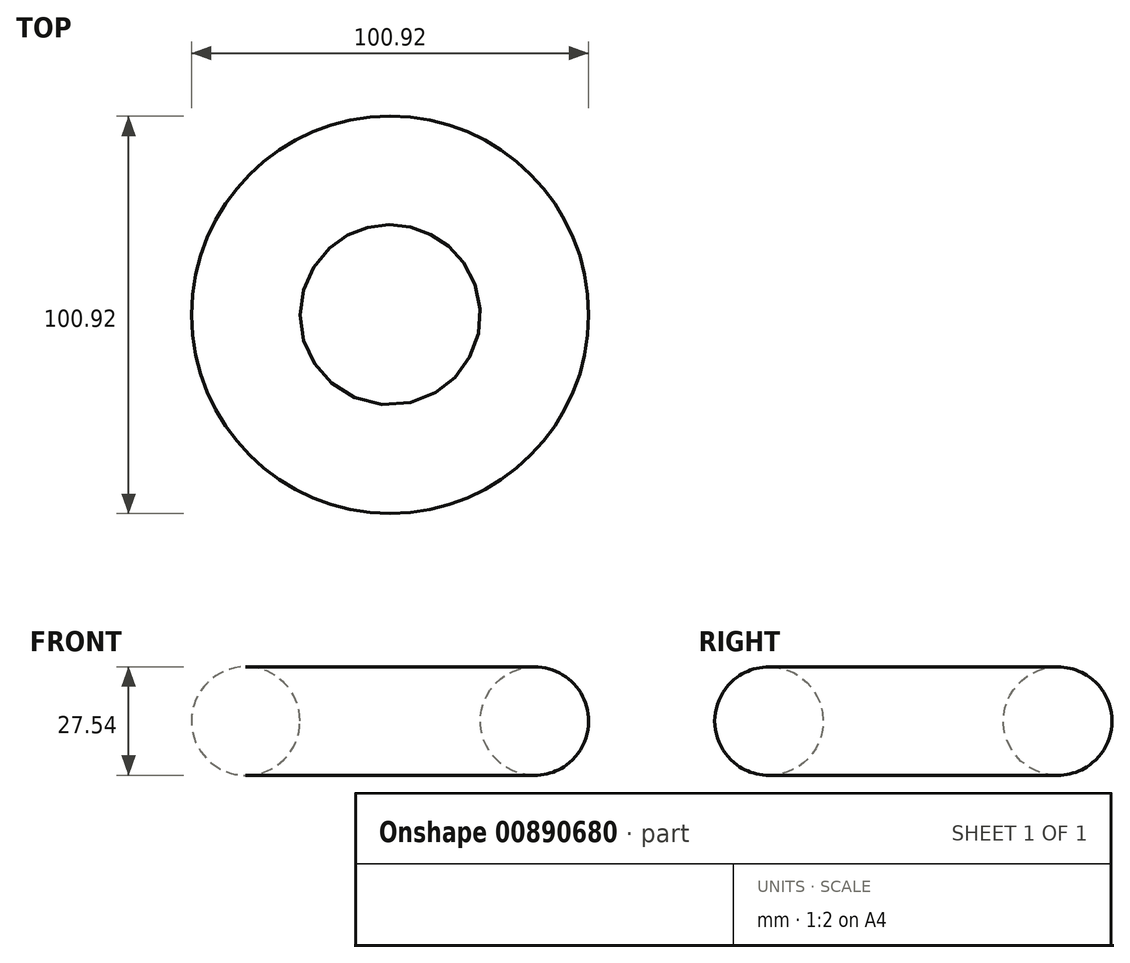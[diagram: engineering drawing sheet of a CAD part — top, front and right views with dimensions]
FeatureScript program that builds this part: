
annotation { "Feature Type Name" : "Feature", "Feature Type Description" : "" }
export const myFeature = defineFeature(function(context is Context, id is Id, definition is map)
    precondition{}
    {
        {
            var Q0;
            Q0=qCreatedBy(makeId("Front.planeOp"),FACE);
            var sketch = newSketch(context, id + "F0", { "sketchPlane" : qUnion([Q0])});
            skCircle(sketch, "E0", {"center": v(36.68, 0) * mm, "radius": 13.77 * mm});
            skSolve(sketch);
        }
        {
            var Q0;
            Q0=qCreatedBy(makeId("Front.planeOp"),FACE);
            var sketch = newSketch(context, id + "F1", { "sketchPlane" : qUnion([Q0])});
            skLineSegment(sketch, "E1", {"start": v(0, 0) * mm, "end": v(0, 25.78) * mm});
            skSolve(sketch);
        }
        {
            var Q0;
            Q0=makeQuery(id+"F0.imprint","IMPRINT",FACE,{"disambiguationData":[TD([[makeQuery(id+"F0.imprint","IMPRINT",EDGE,{"derivedFrom":sQuery(id+"F0.wireOp",EDGE,"E0")}),1.0]])]});
            var Q1;
            Q1=sQuery(id+"F1.wireOp",EDGE,"E1");
            revolve(context, id + "F2", {"surfaceOperationType" : NewSurfaceOperationType.NEW, "entities" : qUnion([Q0]), "axis" : qUnion([Q1]), "revolveType" : RevolveType.FULL});
        }
    });
